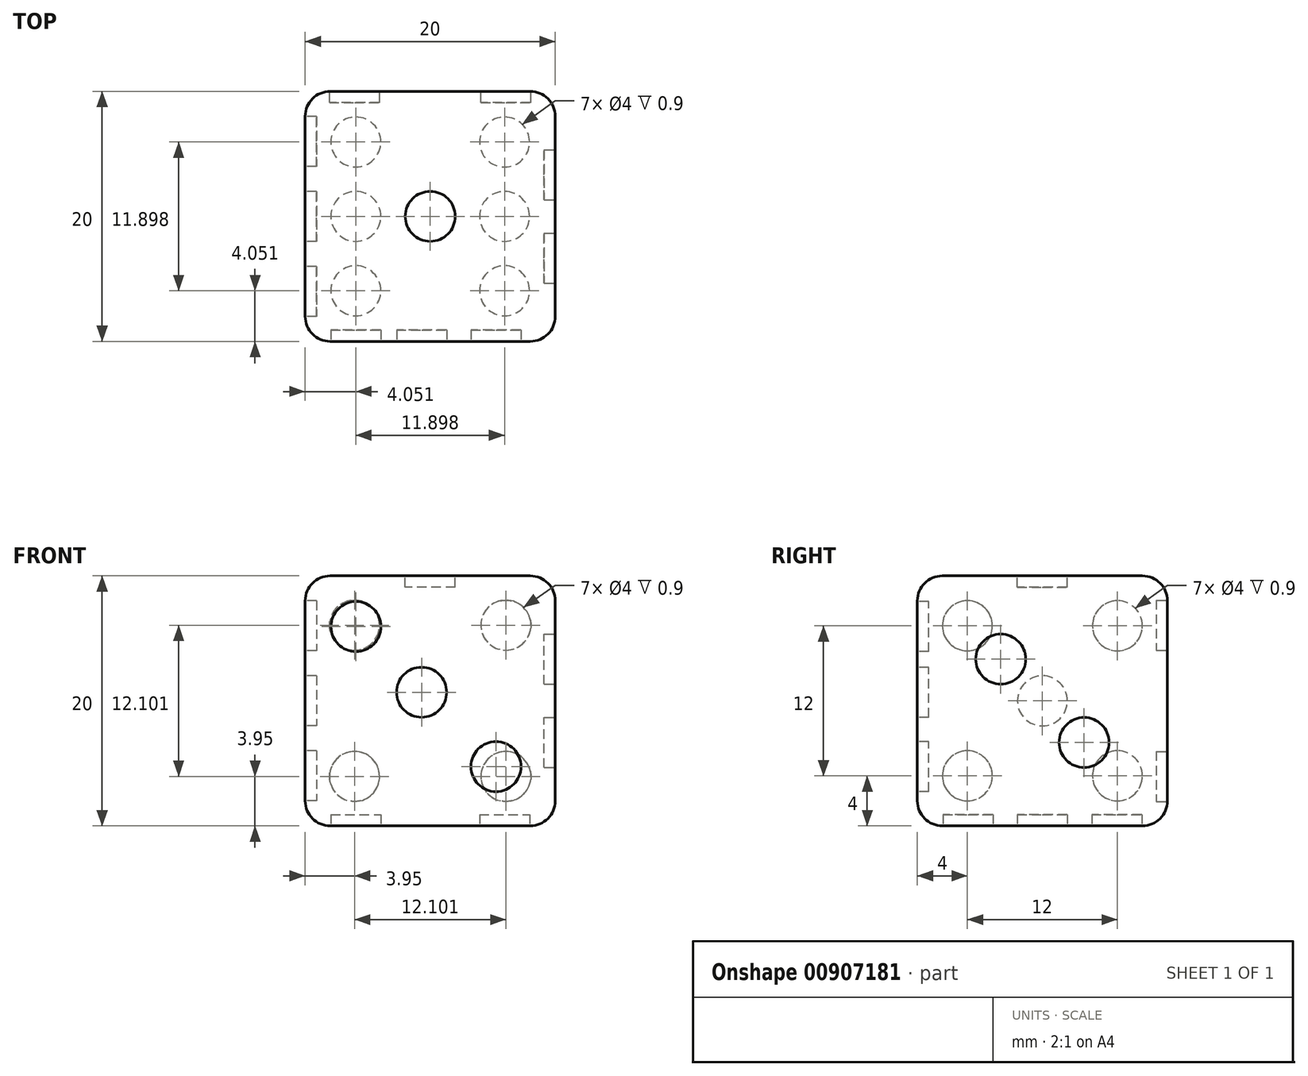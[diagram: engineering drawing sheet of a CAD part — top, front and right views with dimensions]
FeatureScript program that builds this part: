
annotation { "Feature Type Name" : "Feature", "Feature Type Description" : "" }
export const myFeature = defineFeature(function(context is Context, id is Id, definition is map)
    precondition{}
    {
        {
            var Q0;
            Q0=qCreatedBy(makeId("Top.planeOp"),FACE);
            var sketch = newSketch(context, id + "F0", { "sketchPlane" : qUnion([Q0])});
            skLineSegment(sketch, "E0.bottom", {"start": v(0, 0) * mm, "end": v(20, 0) * mm});
            skLineSegment(sketch, "E0.top", {"start": v(0, 20) * mm, "end": v(20, 20) * mm});
            skLineSegment(sketch, "E0.left", {"start": v(0, 0) * mm, "end": v(0, 20) * mm});
            skLineSegment(sketch, "E0.right", {"start": v(20, 0) * mm, "end": v(20, 20) * mm});
            skSolve(sketch);
        }
        {
            var Q0;
            Q0=makeQuery(id+"F0.imprint","IMPRINT",FACE,{"disambiguationData":[TD([[makeQuery(id+"F0.imprint","IMPRINT",EDGE,{"derivedFrom":sQuery(id+"F0.wireOp",EDGE,"E0.bottom")}),1.0]])]});
            extrude(context, id + "F1", {"entities" : qUnion([Q0]), "depth" : 20 * mm, "offsetDistance" : 25 * mm});
        }
        {
            var Q0;
            Q0=makeQuery(id+"F1.opExtrude","CAP_FACE",FACE,{"disambiguationData":[OSD([sQuery(id+"F0.wireOp",EDGE,"E0.bottom"),sQuery(id+"F0.wireOp",EDGE,"E0.top"),sQuery(id+"F0.wireOp",EDGE,"E0.left"),sQuery(id+"F0.wireOp",EDGE,"E0.right")])],"isStart":false});
            var sketch = newSketch(context, id + "F2", { "sketchPlane" : qUnion([Q0])});
            skLineSegment(sketch, "E1", {"start": v(0, 20) * mm, "end": v(20, 0) * mm, "construction": true});
            skLineSegment(sketch, "E2", {"start": v(20, 20) * mm, "end": v(0, 0) * mm, "construction": true});
            skCircle(sketch, "E3", {"center": v(10, 10) * mm, "radius": 2 * mm});
            skSolve(sketch);
        }
        {
            var Q0;
            Q0=makeQuery(id+"F1.opExtrude","CAP_FACE",FACE,{"disambiguationData":[OSD([sQuery(id+"F0.wireOp",EDGE,"E0.bottom"),sQuery(id+"F0.wireOp",EDGE,"E0.top"),sQuery(id+"F0.wireOp",EDGE,"E0.left"),sQuery(id+"F0.wireOp",EDGE,"E0.right")])],"isStart":true});
            var sketch = newSketch(context, id + "F3", { "sketchPlane" : qUnion([Q0])});
            skLineSegment(sketch, "E4", {"start": v(20, -20) * mm, "end": v(0, 0) * mm, "construction": true});
            skLineSegment(sketch, "E5", {"start": v(0, -20) * mm, "end": v(20, 0) * mm, "construction": true});
            skLineSegment(sketch, "E6.bottom", {"start": v(15.95, -4.05) * mm, "end": v(4.05, -4.05) * mm, "construction": true});
            skLineSegment(sketch, "E6.top", {"start": v(15.95, -15.95) * mm, "end": v(4.05, -15.95) * mm, "construction": true});
            skLineSegment(sketch, "E6.left", {"start": v(15.95, -4.05) * mm, "end": v(15.95, -15.95) * mm, "construction": true});
            skLineSegment(sketch, "E6.right", {"start": v(4.05, -4.05) * mm, "end": v(4.05, -15.95) * mm, "construction": true});
            skPoint(sketch, "E6.middle", {"position": v(10, -10) * mm});
            skCircle(sketch, "E7", {"center": v(15.95, -15.95) * mm, "radius": 2 * mm});
            skCircle(sketch, "E8", {"center": v(4.05, -4.05) * mm, "radius": 2 * mm});
            skCircle(sketch, "E9", {"center": v(15.95, -4.05) * mm, "radius": 2 * mm});
            skCircle(sketch, "E10", {"center": v(15.95, -10) * mm, "radius": 2 * mm});
            skCircle(sketch, "E11", {"center": v(4.05, -10) * mm, "radius": 2 * mm});
            skCircle(sketch, "E12", {"center": v(4.05, -15.95) * mm, "radius": 2 * mm});
            skSolve(sketch);
        }
        {
            var Q0;
            Q0=makeQuery(id+"F1.opExtrude","SWEPT_FACE",FACE,{"disambiguationData":[OSD([sQuery(id+"F0.wireOp",EDGE,"E0.right")])]});
            var sketch = newSketch(context, id + "F4", { "sketchPlane" : qUnion([Q0])});
            skCircle(sketch, "E13", {"center": v(6.67, 13.33) * mm, "radius": 2 * mm});
            skCircle(sketch, "E14", {"center": v(13.33, 6.67) * mm, "radius": 2 * mm});
            skLineSegment(sketch, "E15", {"start": v(20, 0) * mm, "end": v(13.33, 6.67) * mm, "construction": true});
            skLineSegment(sketch, "E16", {"start": v(13.33, 6.67) * mm, "end": v(6.67, 13.33) * mm, "construction": true});
            skLineSegment(sketch, "E17", {"start": v(6.67, 13.33) * mm, "end": v(0, 20) * mm, "construction": true});
            skSolve(sketch);
        }
        {
            var Q0;
            Q0=makeQuery(id+"F1.opExtrude","SWEPT_FACE",FACE,{"disambiguationData":[OSD([sQuery(id+"F0.wireOp",EDGE,"E0.left")])]});
            var sketch = newSketch(context, id + "F5", { "sketchPlane" : qUnion([Q0])});
            skLineSegment(sketch, "E18", {"start": v(-20, 20) * mm, "end": v(0, 0) * mm, "construction": true});
            skLineSegment(sketch, "E19", {"start": v(0, 20) * mm, "end": v(-20, 0) * mm, "construction": true});
            skLineSegment(sketch, "E20.bottom", {"start": v(-4, 4) * mm, "end": v(-16, 4) * mm, "construction": true});
            skLineSegment(sketch, "E20.top", {"start": v(-4, 16) * mm, "end": v(-16, 16) * mm, "construction": true});
            skLineSegment(sketch, "E20.left", {"start": v(-4, 4) * mm, "end": v(-4, 16) * mm, "construction": true});
            skLineSegment(sketch, "E20.right", {"start": v(-16, 4) * mm, "end": v(-16, 16) * mm, "construction": true});
            skPoint(sketch, "E20.middle", {"position": v(-10, 10) * mm});
            skCircle(sketch, "E21", {"center": v(-10, 10) * mm, "radius": 2 * mm});
            skCircle(sketch, "E22", {"center": v(-4, 16) * mm, "radius": 2 * mm});
            skCircle(sketch, "E23", {"center": v(-4, 4) * mm, "radius": 2 * mm});
            skCircle(sketch, "E24", {"center": v(-16, 4) * mm, "radius": 2 * mm});
            skCircle(sketch, "E25", {"center": v(-16, 16) * mm, "radius": 2 * mm});
            skSolve(sketch);
        }
        {
            var Q0;
            Q0=makeQuery(id+"F1.opExtrude","SWEPT_FACE",FACE,{"disambiguationData":[OSD([sQuery(id+"F0.wireOp",EDGE,"E0.bottom")])]});
            var sketch = newSketch(context, id + "F6", { "sketchPlane" : qUnion([Q0])});
            skCircle(sketch, "E26", {"center": v(4.06, 15.94) * mm, "radius": 2 * mm});
            skCircle(sketch, "E27", {"center": v(9.31, 10.69) * mm, "radius": 2 * mm});
            skCircle(sketch, "E28", {"center": v(15.26, 4.74) * mm, "radius": 2 * mm});
            skLineSegment(sketch, "E29", {"start": v(0, 20) * mm, "end": v(4.06, 15.94) * mm});
            skLineSegment(sketch, "E30", {"start": v(4.06, 15.94) * mm, "end": v(9.31, 10.69) * mm});
            skLineSegment(sketch, "E31", {"start": v(9.31, 10.69) * mm, "end": v(15.26, 4.74) * mm});
            skLineSegment(sketch, "E32", {"start": v(15.26, 4.74) * mm, "end": v(20, 0) * mm});
            skSolve(sketch);
        }
        {
            var Q0;
            Q0=makeQuery(id+"F1.opExtrude","SWEPT_FACE",FACE,{"disambiguationData":[OSD([sQuery(id+"F0.wireOp",EDGE,"E0.top")])]});
            var sketch = newSketch(context, id + "F7", { "sketchPlane" : qUnion([Q0])});
            skLineSegment(sketch, "E33", {"start": v(0, 20) * mm, "end": v(-20, 0) * mm, "construction": true});
            skLineSegment(sketch, "E34", {"start": v(0, 0) * mm, "end": v(-20, 20) * mm, "construction": true});
            skLineSegment(sketch, "E35.bottom", {"start": v(-16.05, 16.05) * mm, "end": v(-3.95, 16.05) * mm, "construction": true});
            skLineSegment(sketch, "E35.top", {"start": v(-16.05, 3.95) * mm, "end": v(-3.95, 3.95) * mm, "construction": true});
            skLineSegment(sketch, "E35.left", {"start": v(-16.05, 16.05) * mm, "end": v(-16.05, 3.95) * mm, "construction": true});
            skLineSegment(sketch, "E35.right", {"start": v(-3.95, 16.05) * mm, "end": v(-3.95, 3.95) * mm, "construction": true});
            skPoint(sketch, "E35.middle", {"position": v(-10, 10) * mm});
            skCircle(sketch, "E36", {"center": v(-3.95, 16.05) * mm, "radius": 2 * mm});
            skCircle(sketch, "E37", {"center": v(-3.95, 3.95) * mm, "radius": 2 * mm});
            skCircle(sketch, "E38", {"center": v(-16.05, 3.95) * mm, "radius": 2 * mm});
            skCircle(sketch, "E39", {"center": v(-16.05, 16.05) * mm, "radius": 2 * mm});
            skSolve(sketch);
        }
        {
            var Q0;
            Q0=makeQuery(id+"F5.imprint","IMPRINT",FACE,{"disambiguationData":[TD([[makeQuery(id+"F5.imprint","IMPRINT",EDGE,{"derivedFrom":sQuery(id+"F5.wireOp",EDGE,"E25")}),1.0]])]});
            var Q1;
            Q1=makeQuery(id+"F5.imprint","IMPRINT",FACE,{"disambiguationData":[TD([[makeQuery(id+"F5.imprint","IMPRINT",EDGE,{"derivedFrom":sQuery(id+"F5.wireOp",EDGE,"E21")}),1.0]])]});
            var Q2;
            Q2=makeQuery(id+"F5.imprint","IMPRINT",FACE,{"disambiguationData":[TD([[makeQuery(id+"F5.imprint","IMPRINT",EDGE,{"derivedFrom":sQuery(id+"F5.wireOp",EDGE,"E22")}),1.0]])]});
            var Q3;
            Q3=makeQuery(id+"F5.imprint","IMPRINT",FACE,{"disambiguationData":[TD([[makeQuery(id+"F5.imprint","IMPRINT",EDGE,{"derivedFrom":sQuery(id+"F5.wireOp",EDGE,"E23")}),1.0]])]});
            var Q4;
            Q4=makeQuery(id+"F5.imprint","IMPRINT",FACE,{"disambiguationData":[TD([[makeQuery(id+"F5.imprint","IMPRINT",EDGE,{"derivedFrom":sQuery(id+"F5.wireOp",EDGE,"E24")}),1.0]])]});
            extrude(context, id + "F8", {"entities" : qUnion([Q0, Q1, Q2, Q3, Q4]), "operationType" : NewBodyOperationType.REMOVE, "oppositeDirection" : true, "depth" : .9 * mm, "offsetDistance" : 25 * mm});
        }
        {
            var Q0;
            Q0=makeQuery(id+"F2.imprint","IMPRINT",FACE,{"disambiguationData":[TD([[makeQuery(id+"F2.imprint","IMPRINT",EDGE,{"derivedFrom":sQuery(id+"F2.wireOp",EDGE,"E3")}),1.0]])]});
            extrude(context, id + "F9", {"entities" : qUnion([Q0]), "operationType" : NewBodyOperationType.REMOVE, "oppositeDirection" : true, "depth" : .9 * mm, "offsetDistance" : 25 * mm});
        }
        {
            var Q0;
            Q0=makeQuery(id+"F4.imprint","IMPRINT",FACE,{"disambiguationData":[TD([[makeQuery(id+"F4.imprint","IMPRINT",EDGE,{"derivedFrom":sQuery(id+"F4.wireOp",EDGE,"E14")}),1.0]])]});
            var Q1;
            Q1=makeQuery(id+"F4.imprint","IMPRINT",FACE,{"disambiguationData":[TD([[makeQuery(id+"F4.imprint","IMPRINT",EDGE,{"derivedFrom":sQuery(id+"F4.wireOp",EDGE,"E13")}),1.0]])]});
            extrude(context, id + "F10", {"entities" : qUnion([Q0, Q1]), "operationType" : NewBodyOperationType.REMOVE, "oppositeDirection" : true, "depth" : .9 * mm, "offsetDistance" : 25 * mm});
        }
        {
            var Q0;
            Q0=makeQuery(id+"F7.imprint","IMPRINT",FACE,{"disambiguationData":[TD([[makeQuery(id+"F7.imprint","IMPRINT",EDGE,{"derivedFrom":sQuery(id+"F7.wireOp",EDGE,"E36")}),1.0]])]});
            var Q1;
            Q1=makeQuery(id+"F7.imprint","IMPRINT",FACE,{"disambiguationData":[TD([[makeQuery(id+"F7.imprint","IMPRINT",EDGE,{"derivedFrom":sQuery(id+"F7.wireOp",EDGE,"E37")}),1.0]])]});
            var Q2;
            Q2=makeQuery(id+"F7.imprint","IMPRINT",FACE,{"disambiguationData":[TD([[makeQuery(id+"F7.imprint","IMPRINT",EDGE,{"derivedFrom":sQuery(id+"F7.wireOp",EDGE,"E38")}),1.0]])]});
            var Q3;
            Q3=makeQuery(id+"F7.imprint","IMPRINT",FACE,{"disambiguationData":[TD([[makeQuery(id+"F7.imprint","IMPRINT",EDGE,{"derivedFrom":sQuery(id+"F7.wireOp",EDGE,"E39")}),1.0]])]});
            extrude(context, id + "F11", {"entities" : qUnion([Q0, Q1, Q2, Q3]), "operationType" : NewBodyOperationType.REMOVE, "oppositeDirection" : true, "depth" : .9 * mm, "offsetDistance" : 25 * mm});
        }
        {
            var Q0;
            {var subQ0=sQuery(id+"F6.wireOp",EDGE,"E31");var subQ1=sQuery(id+"F6.wireOp",EDGE,"E28");var subQ2=makeQuery(id+"F6.imprint","INTERSECT",VERTEX,{"derivedFrom":[subQ1,subQ0]});Q0=makeQuery(id+"F6.imprint","IMPRINT",FACE,{"disambiguationData":[TD([[makeQuery(id+"F6.imprint","IMPRINT",EDGE,{"disambiguationData":[TD([[subQ2,-1.0]])],"derivedFrom":subQ1}),1.0]])]});}
            var Q1;
            {var subQ0=sQuery(id+"F6.wireOp",EDGE,"E31");var subQ1=sQuery(id+"F6.wireOp",EDGE,"E28");var subQ2=makeQuery(id+"F6.imprint","INTERSECT",VERTEX,{"derivedFrom":[subQ1,subQ0]});Q1=makeQuery(id+"F6.imprint","IMPRINT",FACE,{"disambiguationData":[TD([[makeQuery(id+"F6.imprint","IMPRINT",EDGE,{"disambiguationData":[TD([[subQ2,1.0]])],"derivedFrom":subQ1}),1.0]])]});}
            var Q2;
            {var subQ0=sQuery(id+"F6.wireOp",EDGE,"E30");var subQ1=sQuery(id+"F6.wireOp",EDGE,"E27");var subQ2=makeQuery(id+"F6.imprint","INTERSECT",VERTEX,{"derivedFrom":[subQ1,subQ0]});Q2=makeQuery(id+"F6.imprint","IMPRINT",FACE,{"disambiguationData":[TD([[makeQuery(id+"F6.imprint","IMPRINT",EDGE,{"disambiguationData":[TD([[subQ2,1.0]])],"derivedFrom":subQ1}),1.0]])]});}
            var Q3;
            {var subQ0=sQuery(id+"F6.wireOp",EDGE,"E30");var subQ1=sQuery(id+"F6.wireOp",EDGE,"E27");var subQ2=makeQuery(id+"F6.imprint","INTERSECT",VERTEX,{"derivedFrom":[subQ1,subQ0]});Q3=makeQuery(id+"F6.imprint","IMPRINT",FACE,{"disambiguationData":[TD([[makeQuery(id+"F6.imprint","IMPRINT",EDGE,{"disambiguationData":[TD([[subQ2,-1.0]])],"derivedFrom":subQ1}),1.0]])]});}
            var Q4;
            {var subQ0=sQuery(id+"F6.wireOp",EDGE,"E29");var subQ1=sQuery(id+"F6.wireOp",EDGE,"E26");var subQ2=makeQuery(id+"F6.imprint","INTERSECT",VERTEX,{"derivedFrom":[subQ1,subQ0]});Q4=makeQuery(id+"F6.imprint","IMPRINT",FACE,{"disambiguationData":[TD([[makeQuery(id+"F6.imprint","IMPRINT",EDGE,{"disambiguationData":[TD([[subQ2,1.0]])],"derivedFrom":subQ1}),1.0]])]});}
            var Q5;
            {var subQ0=sQuery(id+"F6.wireOp",EDGE,"E29");var subQ1=sQuery(id+"F6.wireOp",EDGE,"E26");var subQ2=makeQuery(id+"F6.imprint","INTERSECT",VERTEX,{"derivedFrom":[subQ1,subQ0]});Q5=makeQuery(id+"F6.imprint","IMPRINT",FACE,{"disambiguationData":[TD([[makeQuery(id+"F6.imprint","IMPRINT",EDGE,{"disambiguationData":[TD([[subQ2,-1.0]])],"derivedFrom":subQ1}),1.0]])]});}
            extrude(context, id + "F12", {"entities" : qUnion([Q0, Q1, Q2, Q3, Q4, Q5]), "operationType" : NewBodyOperationType.REMOVE, "oppositeDirection" : true, "depth" : .9 * mm, "offsetDistance" : 25 * mm});
        }
        {
            var Q0;
            Q0=makeQuery(id+"F3.imprint","IMPRINT",FACE,{"disambiguationData":[TD([[makeQuery(id+"F3.imprint","IMPRINT",EDGE,{"derivedFrom":sQuery(id+"F3.wireOp",EDGE,"E9")}),1.0]])]});
            var Q1;
            Q1=makeQuery(id+"F3.imprint","IMPRINT",FACE,{"disambiguationData":[TD([[makeQuery(id+"F3.imprint","IMPRINT",EDGE,{"derivedFrom":sQuery(id+"F3.wireOp",EDGE,"E10")}),1.0]])]});
            var Q2;
            Q2=makeQuery(id+"F3.imprint","IMPRINT",FACE,{"disambiguationData":[TD([[makeQuery(id+"F3.imprint","IMPRINT",EDGE,{"derivedFrom":sQuery(id+"F3.wireOp",EDGE,"E7")}),1.0]])]});
            var Q3;
            Q3=makeQuery(id+"F3.imprint","IMPRINT",FACE,{"disambiguationData":[TD([[makeQuery(id+"F3.imprint","IMPRINT",EDGE,{"derivedFrom":sQuery(id+"F3.wireOp",EDGE,"E8")}),1.0]])]});
            var Q4;
            Q4=makeQuery(id+"F3.imprint","IMPRINT",FACE,{"disambiguationData":[TD([[makeQuery(id+"F3.imprint","IMPRINT",EDGE,{"derivedFrom":sQuery(id+"F3.wireOp",EDGE,"E11")}),1.0]])]});
            var Q5;
            Q5=makeQuery(id+"F3.imprint","IMPRINT",FACE,{"disambiguationData":[TD([[makeQuery(id+"F3.imprint","IMPRINT",EDGE,{"derivedFrom":sQuery(id+"F3.wireOp",EDGE,"E12")}),1.0]])]});
            extrude(context, id + "F13", {"entities" : qUnion([Q0, Q1, Q2, Q3, Q4, Q5]), "operationType" : NewBodyOperationType.REMOVE, "oppositeDirection" : true, "depth" : .9 * mm, "offsetDistance" : 25 * mm});
        }
        {
            var Q0;
            Q0=makeQuery(id+"F1.opExtrude","CAP_EDGE",EDGE,{"disambiguationData":[OSD([sQuery(id+"F0.wireOp",EDGE,"E0.right")])],"isStart":true});
            var Q1;
            Q1=makeQuery(id+"F1.opExtrude","CAP_EDGE",EDGE,{"disambiguationData":[OSD([sQuery(id+"F0.wireOp",EDGE,"E0.top")])],"isStart":true});
            var Q2;
            Q2=makeQuery(id+"F1.opExtrude","SWEPT_EDGE",EDGE,{"disambiguationData":[OSD([sQuery(id+"F0.wireOp",EDGE,"E0.top"),sQuery(id+"F0.wireOp",EDGE,"E0.left")])]});
            var Q3;
            Q3=makeQuery(id+"F1.opExtrude","CAP_EDGE",EDGE,{"disambiguationData":[OSD([sQuery(id+"F0.wireOp",EDGE,"E0.left")])],"isStart":false});
            var Q4;
            Q4=makeQuery(id+"F1.opExtrude","CAP_EDGE",EDGE,{"disambiguationData":[OSD([sQuery(id+"F0.wireOp",EDGE,"E0.top")])],"isStart":false});
            var Q5;
            Q5=makeQuery(id+"F1.opExtrude","CAP_EDGE",EDGE,{"disambiguationData":[OSD([sQuery(id+"F0.wireOp",EDGE,"E0.right")])],"isStart":false});
            var Q6;
            Q6=makeQuery(id+"F1.opExtrude","SWEPT_EDGE",EDGE,{"disambiguationData":[OSD([sQuery(id+"F0.wireOp",EDGE,"E0.bottom"),sQuery(id+"F0.wireOp",EDGE,"E0.right")])]});
            var Q7;
            Q7=makeQuery(id+"F1.opExtrude","CAP_EDGE",EDGE,{"disambiguationData":[OSD([sQuery(id+"F0.wireOp",EDGE,"E0.bottom")])],"isStart":false});
            var Q8;
            Q8=makeQuery(id+"F1.opExtrude","SWEPT_EDGE",EDGE,{"disambiguationData":[OSD([sQuery(id+"F0.wireOp",EDGE,"E0.top"),sQuery(id+"F0.wireOp",EDGE,"E0.right")])]});
            var Q9;
            Q9=makeQuery(id+"F1.opExtrude","CAP_EDGE",EDGE,{"disambiguationData":[OSD([sQuery(id+"F0.wireOp",EDGE,"E0.left")])],"isStart":true});
            var Q10;
            Q10=makeQuery(id+"F1.opExtrude","SWEPT_EDGE",EDGE,{"disambiguationData":[OSD([sQuery(id+"F0.wireOp",EDGE,"E0.bottom"),sQuery(id+"F0.wireOp",EDGE,"E0.left")])]});
            var Q11;
            Q11=makeQuery(id+"F1.opExtrude","CAP_EDGE",EDGE,{"disambiguationData":[OSD([sQuery(id+"F0.wireOp",EDGE,"E0.bottom")])],"isStart":true});
            fillet(context, id + "F14", {"entities" : qUnion([Q0, Q1, Q2, Q3, Q4, Q5, Q6, Q7, Q8, Q9, Q10, Q11]), "radius" : 2 * mm, "tangentPropagation" : true, "allowEdgeOverflow" : false});
        }
    });
